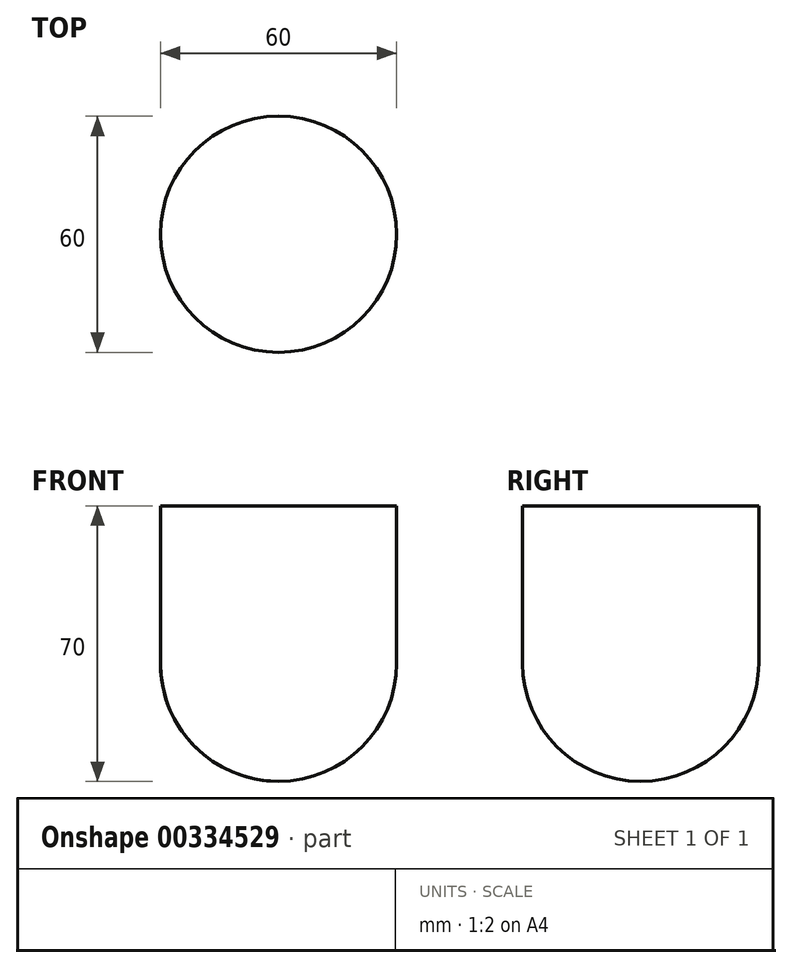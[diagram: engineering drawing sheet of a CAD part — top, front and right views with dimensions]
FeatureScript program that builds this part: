
annotation { "Feature Type Name" : "Feature", "Feature Type Description" : "" }
export const myFeature = defineFeature(function(context is Context, id is Id, definition is map)
    precondition{}
    {
        {
            var Q0;
            Q0=qCreatedBy(makeId("Front.planeOp"),FACE);
            var sketch = newSketch(context, id + "F0", { "sketchPlane" : qUnion([Q0])});
            skLineSegment(sketch, "E0.bottom", {"start": v(0, 70) * mm, "end": v(30, 70) * mm});
            skLineSegment(sketch, "E0.top", {"start": v(0, 30) * mm, "end": v(30, 30) * mm});
            skLineSegment(sketch, "E0.left", {"start": v(0, 70) * mm, "end": v(0, 30) * mm});
            skLineSegment(sketch, "E0.right", {"start": v(30, 70) * mm, "end": v(30, 30) * mm});
            skArc(sketch, "E1", {"start": v(30, 30) * mm, "mid": v(21.21, 8.79) * mm, "end": v(0, 0) * mm});
            skLineSegment(sketch, "E2", {"start": v(0, 30) * mm, "end": v(0, 0) * mm});
            skLineSegment(sketch, "E3", {"start": v(0, 70) * mm, "end": v(-15.84, 70) * mm, "construction": true});
            skLineSegment(sketch, "E4", {"start": v(0, 0) * mm, "end": v(0, -28.93) * mm, "construction": true});
            skSolve(sketch);
        }
        {
            var Q0;
            Q0=makeQuery(id+"F0.imprint","IMPRINT",FACE,{"disambiguationData":[TD([[makeQuery(id+"F0.imprint","IMPRINT",EDGE,{"derivedFrom":sQuery(id+"F0.wireOp",EDGE,"7f847dba-da7f-440c-a909-31c7d03b6bc5.top")}),-1.0]])]});
            var Q1;
            Q1=makeQuery(id+"F0.imprint","IMPRINT",FACE,{"disambiguationData":[TD([[makeQuery(id+"F0.imprint","IMPRINT",EDGE,{"derivedFrom":sQuery(id+"F0.wireOp",EDGE,"E0.top")}),1.0]])]});
            var Q2;
            Q2=makeQuery(id+"F0.imprint","IMPRINT",FACE,{"disambiguationData":[TD([[makeQuery(id+"F0.imprint","IMPRINT",EDGE,{"derivedFrom":sQuery(id+"F0.wireOp",EDGE,"E0.top")}),-1.0]])]});
            var Q3;
            Q3=sQuery(id+"F0.wireOp",EDGE,"E0.left");
            revolve(context, id + "F1", {"entities" : qUnion([Q0, Q1, Q2]), "axis" : qUnion([Q3]), "revolveType" : RevolveType.FULL});
        }
    });
